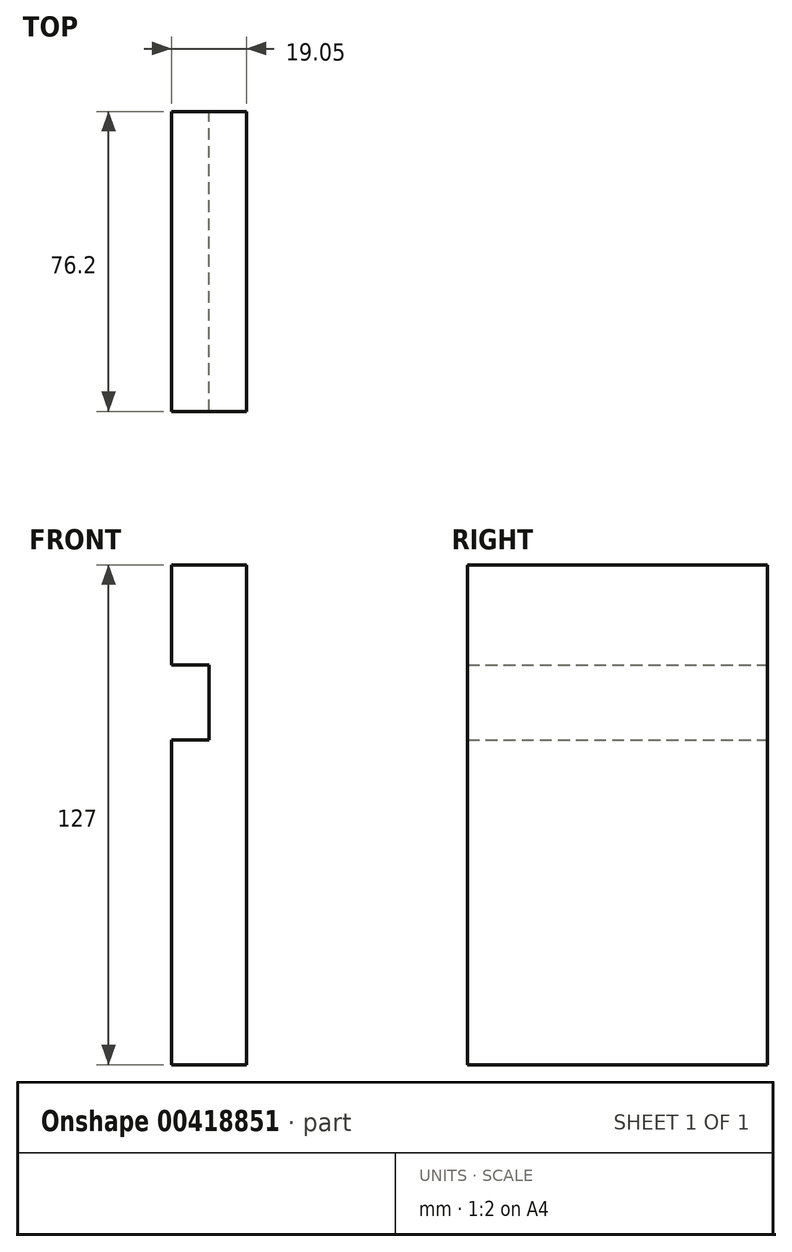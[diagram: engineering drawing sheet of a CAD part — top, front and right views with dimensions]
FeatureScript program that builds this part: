
annotation { "Feature Type Name" : "Feature", "Feature Type Description" : "" }
export const myFeature = defineFeature(function(context is Context, id is Id, definition is map)
    precondition{}
    {
        {
            var Q0;
            Q0=qCreatedBy(makeId("Front.planeOp"),FACE);
            var sketch = newSketch(context, id + "F0", { "sketchPlane" : qUnion([Q0])});
            skLineSegment(sketch, "E0", {"start": v(-21.77, 54.04) * mm, "end": v(-2.72, 54.04) * mm});
            skLineSegment(sketch, "E1", {"start": v(-2.72, 54.04) * mm, "end": v(-2.72, -72.96) * mm});
            skLineSegment(sketch, "E2", {"start": v(-2.72, -72.96) * mm, "end": v(-21.77, -72.96) * mm});
            skLineSegment(sketch, "E3", {"start": v(-21.77, 54.04) * mm, "end": v(-21.77, 28.64) * mm});
            skLineSegment(sketch, "E4", {"start": v(-21.77, 28.64) * mm, "end": v(-12.24, 28.64) * mm});
            skLineSegment(sketch, "E5", {"start": v(-12.24, 28.64) * mm, "end": v(-12.24, 9.6) * mm});
            skLineSegment(sketch, "E6", {"start": v(-12.24, 9.6) * mm, "end": v(-21.77, 9.6) * mm});
            skLineSegment(sketch, "E7", {"start": v(-21.77, 9.6) * mm, "end": v(-21.77, -72.96) * mm});
            skSolve(sketch);
        }
        {
            var Q0;
            Q0 = qSketchRegion(id + "F0", true);
            extrude(context, id + "F1", {"entities" : qUnion([Q0]), "depth" : 76.2 * mm});
        }
    });
